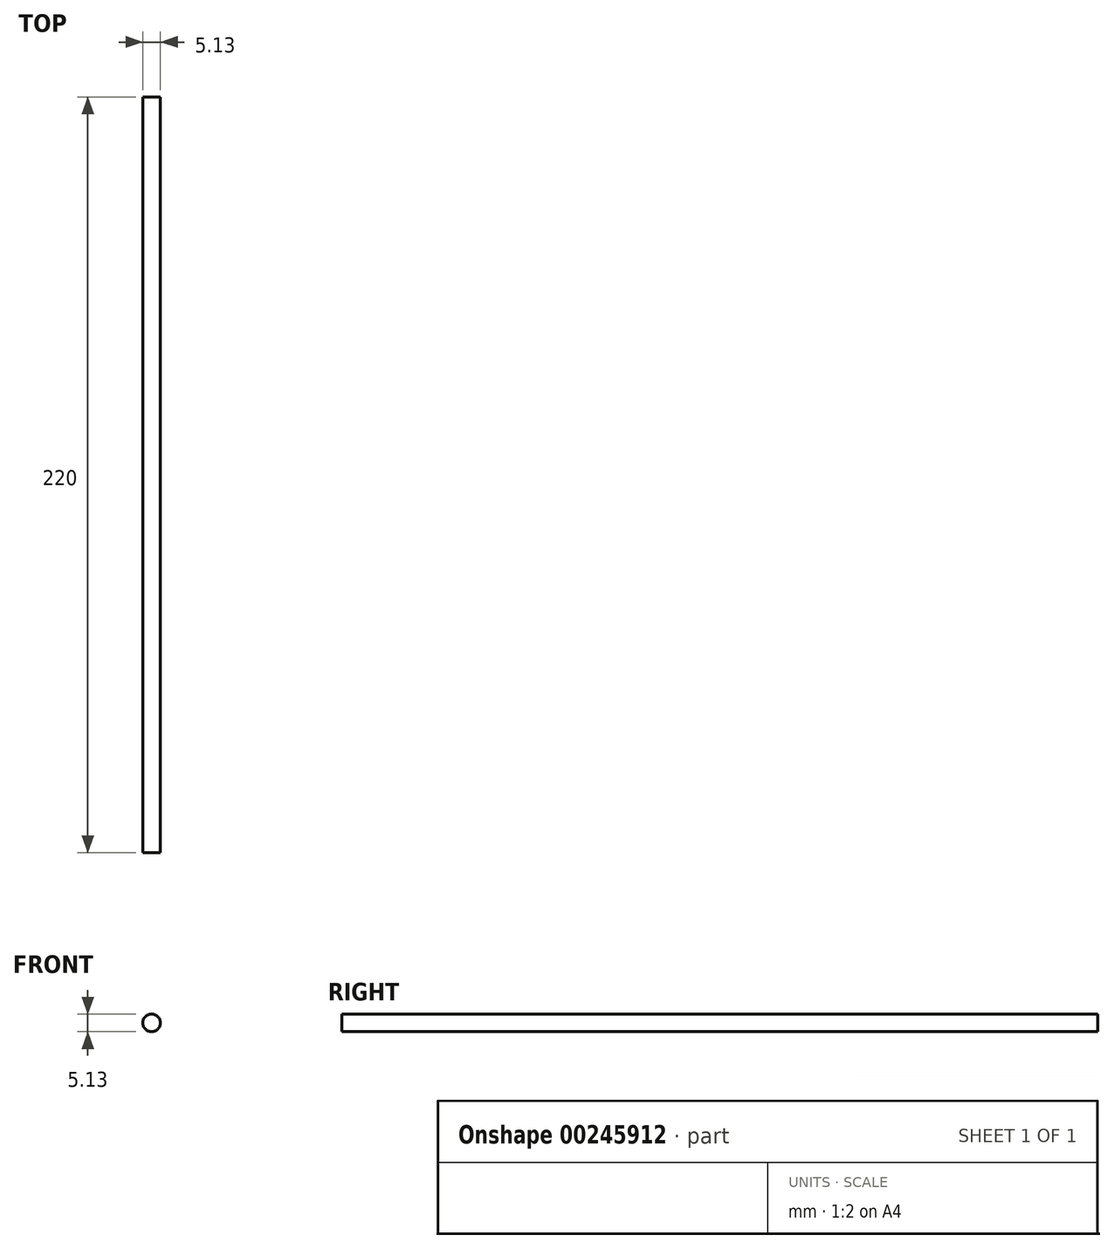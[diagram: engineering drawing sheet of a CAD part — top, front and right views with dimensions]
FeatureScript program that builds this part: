
annotation { "Feature Type Name" : "Feature", "Feature Type Description" : "" }
export const myFeature = defineFeature(function(context is Context, id is Id, definition is map)
    precondition{}
    {
        {
            var Q0;
            Q0=qCreatedBy(makeId("Front.planeOp"),FACE);
            var sketch = newSketch(context, id + "F0", { "sketchPlane" : qUnion([Q0])});
            skCircle(sketch, "E0", {"center": v(-44.14, 44.02) * mm, "radius": 2.57 * mm});
            skSolve(sketch);
        }
        {
            var Q0;
            Q0=makeQuery(id+"F0.imprint","IMPRINT",FACE,{"disambiguationData":[TD([[makeQuery(id+"F0.imprint","IMPRINT",EDGE,{"derivedFrom":sQuery(id+"F0.wireOp",EDGE,"E0")}),1.0]])]});
            extrude(context, id + "F1", {"entities" : qUnion([Q0]), "oppositeDirection" : true, "depth" : 220 * mm});
        }
    });
